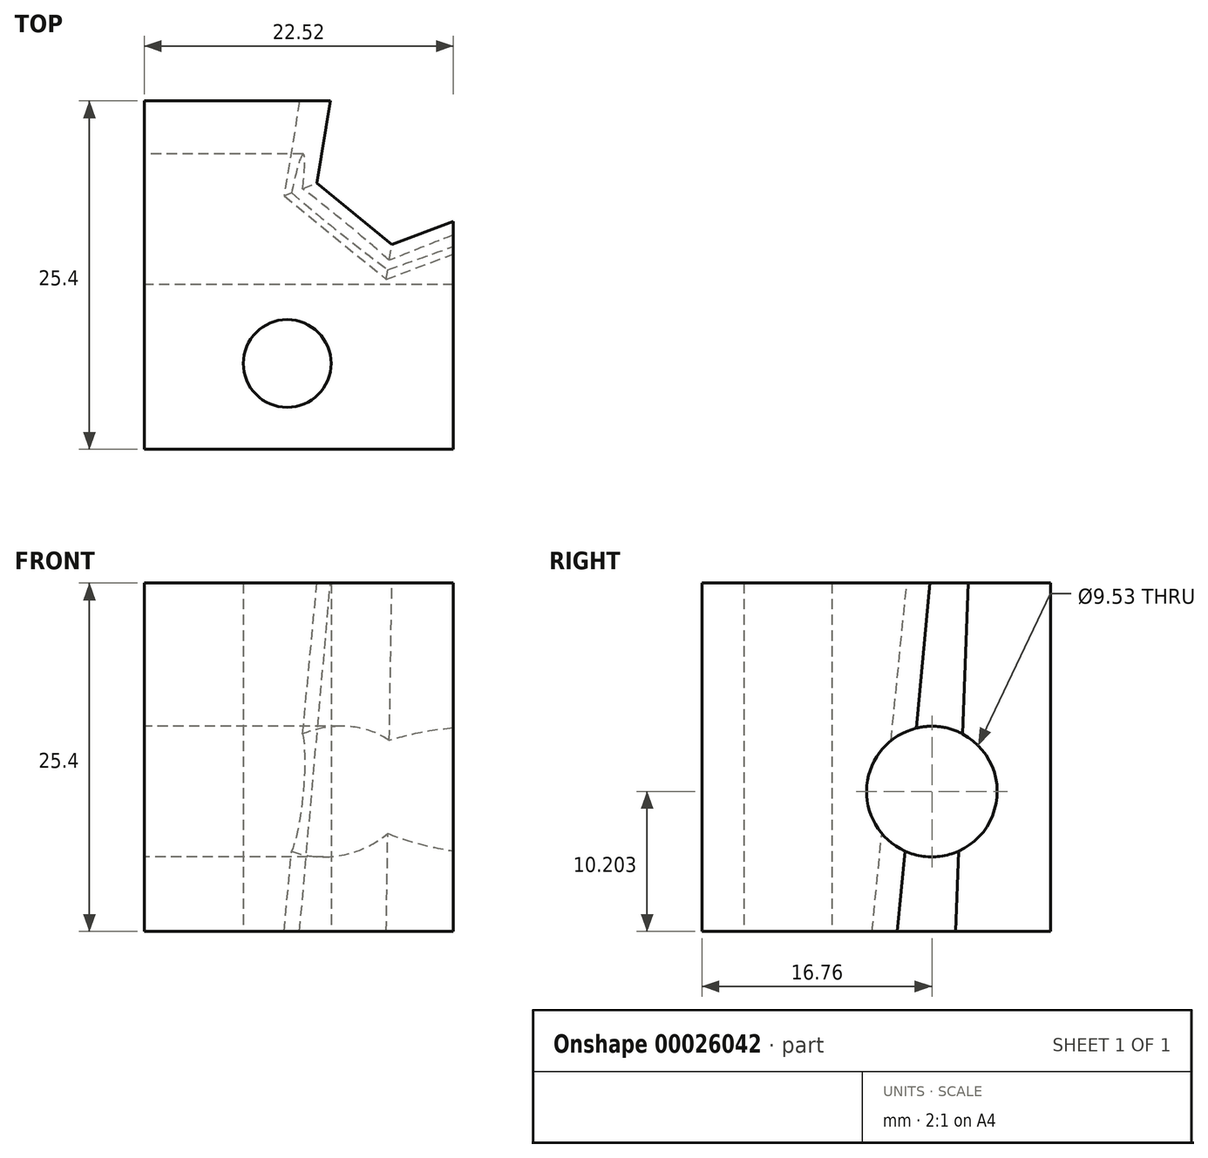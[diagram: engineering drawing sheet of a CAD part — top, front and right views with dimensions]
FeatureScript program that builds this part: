
annotation { "Feature Type Name" : "Feature", "Feature Type Description" : "" }
export const myFeature = defineFeature(function(context is Context, id is Id, definition is map)
    precondition{}
    {
        {
            var Q0;
            Q0=qCreatedBy(makeId("Top.planeOp"),FACE);
            var sketch = newSketch(context, id + "F0", { "sketchPlane" : qUnion([Q0])});
            skLineSegment(sketch, "E0.bottom", {"start": v(0, 0) * mm, "end": v(22.52, 0) * mm});
            skLineSegment(sketch, "E0.top", {"start": v(0, 25.4) * mm, "end": v(22.52, 25.4) * mm});
            skLineSegment(sketch, "E0.left", {"start": v(0, 0) * mm, "end": v(0, 25.4) * mm});
            skLineSegment(sketch, "E0.right", {"start": v(22.52, 0) * mm, "end": v(22.52, 25.4) * mm});
            skCircle(sketch, "E1", {"center": v(10.41, 6.26) * mm, "radius": 3.2 * mm});
            skSolve(sketch);
        }
        {
            var Q0;
            Q0 = qSketchRegion(id + "F0", true);
            extrude(context, id + "F1", {"entities" : qUnion([Q0]), "depth" : 25.4 * mm});
        }
        {
            var Q0;
            Q0=makeQuery(id+"F1.opExtrude","SWEPT_FACE",FACE,{"disambiguationData":[OSD([sQuery(id+"F0.wireOp",EDGE,"E0.left")])]});
            var sketch = newSketch(context, id + "F2", { "sketchPlane" : qUnion([Q0])});
            skLineSegment(sketch, "E2", {"start": v(-9.46, 0) * mm, "end": v(-9.46, 25.4) * mm, "construction": true});
            skLineSegment(sketch, "E3", {"start": v(-12, 25.4) * mm, "end": v(-12, 0) * mm, "construction": true});
            skCircle(sketch, "E4", {"center": v(-16.76, 10.2) * mm, "radius": 4.76 * mm});
            skSolve(sketch);
        }
        {
            var Q0;
            Q0 = qSketchRegion(id + "F2", true);
            extrude(context, id + "F3", {"entities" : qUnion([Q0]), "operationType" : NewBodyOperationType.REMOVE, "endBound" : BoundingType.THROUGH_ALL, "oppositeDirection" : true, "depth" : 25.4 * mm});
        }
        {
            var Q0;
            Q0=makeQuery(id+"F1.opExtrude","CAP_FACE",FACE,{"disambiguationData":[OSD([sQuery(id+"F0.wireOp",EDGE,"E0.bottom"),sQuery(id+"F0.wireOp",EDGE,"E0.top"),sQuery(id+"F0.wireOp",EDGE,"E0.left"),sQuery(id+"F0.wireOp",EDGE,"E0.right"),sQuery(id+"F0.wireOp",EDGE,"E1")])],"isStart":false});
            var sketch = newSketch(context, id + "F4", { "sketchPlane" : qUnion([Q0])});
            skCircle(sketch, "E5.cCircle", {"center": v(19.19, 21.9) * mm, "radius": 6.12 * mm, "construction": true});
            skLineSegment(sketch, "E5.0", {"start": v(25.8, 24.39) * mm, "end": v(24.65, 17.42) * mm});
            skLineSegment(sketch, "E5.1", {"start": v(24.65, 17.42) * mm, "end": v(18.05, 14.92) * mm});
            skLineSegment(sketch, "E5.2", {"start": v(18.05, 14.92) * mm, "end": v(12.58, 19.4) * mm});
            skLineSegment(sketch, "E5.3", {"start": v(12.58, 19.4) * mm, "end": v(13.72, 26.37) * mm});
            skLineSegment(sketch, "E5.4", {"start": v(13.72, 26.37) * mm, "end": v(20.33, 28.86) * mm});
            skLineSegment(sketch, "E5.5", {"start": v(20.33, 28.86) * mm, "end": v(25.8, 24.39) * mm});
            skPoint(sketch, "E5.0.midPoint", {"position": v(25.22, 20.9) * mm});
            skSolve(sketch);
        }
        {
            var Q0;
            Q0 = qSketchRegion(id + "F4", true);
            extrude(context, id + "F5", {"entities" : qUnion([Q0]), "operationType" : NewBodyOperationType.REMOVE, "endBound" : BoundingType.THROUGH_ALL, "oppositeDirection" : true, "depth" : 25.4 * mm, "offsetDistance" : 25.4 * mm, "hasDraft" : true, "draftAngle" : 5 * degree});
        }
    });
